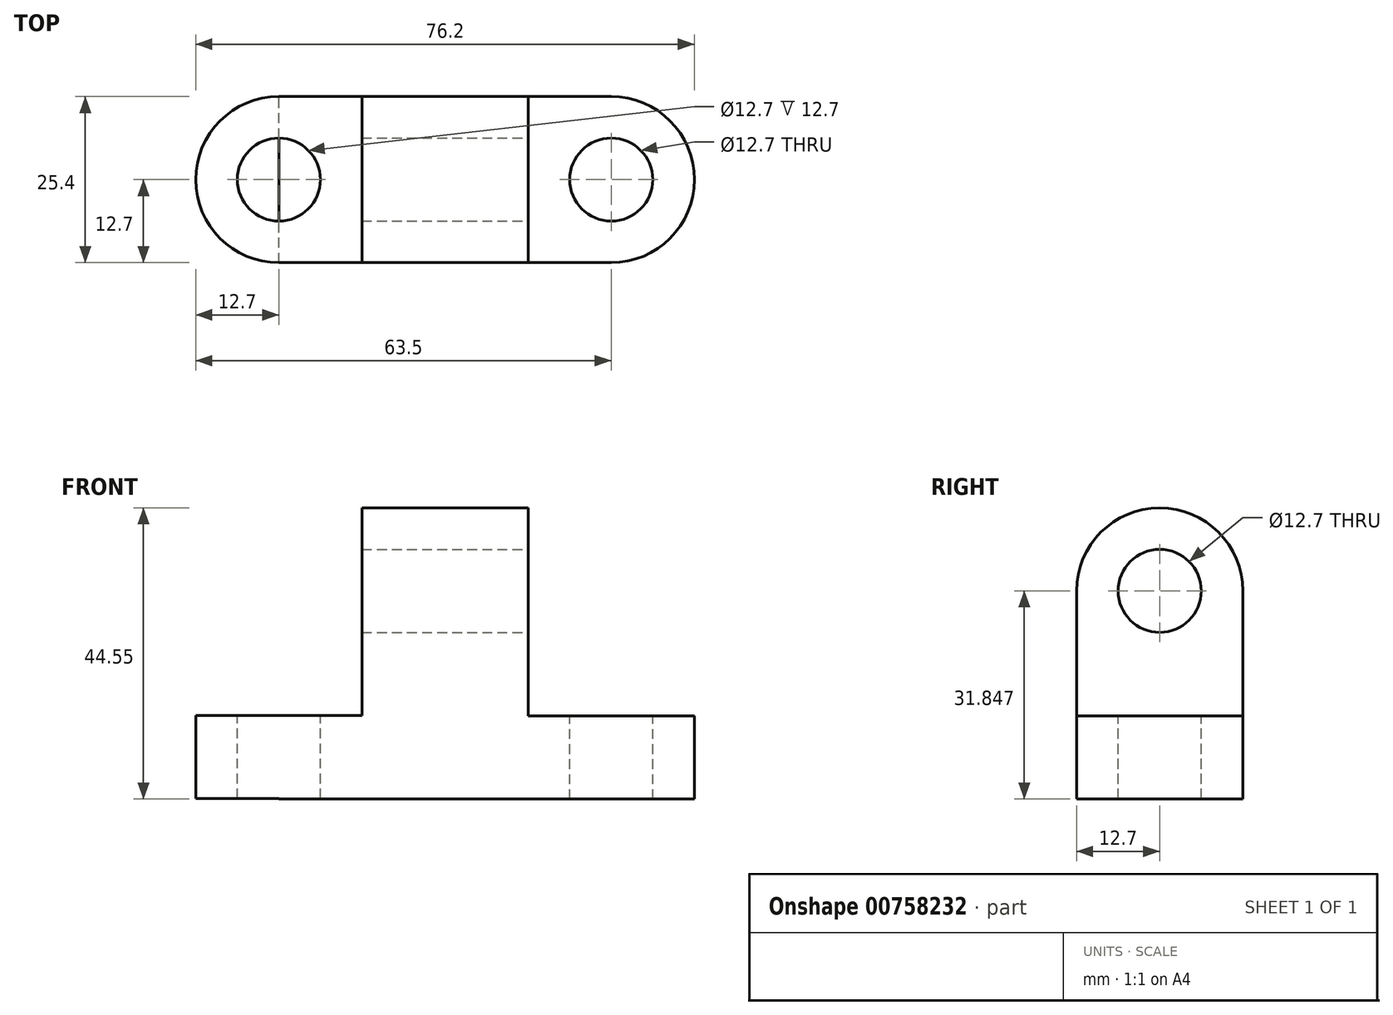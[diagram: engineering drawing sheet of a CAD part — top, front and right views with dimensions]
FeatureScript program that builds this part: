
annotation { "Feature Type Name" : "Feature", "Feature Type Description" : "" }
export const myFeature = defineFeature(function(context is Context, id is Id, definition is map)
    precondition{}
    {
        {
            var Q0;
            Q0=qCreatedBy(makeId("Front.planeOp"),FACE);
            var sketch = newSketch(context, id + "F0", { "sketchPlane" : qUnion([Q0])});
            skLineSegment(sketch, "E0", {"start": v(0, 0) * mm, "end": v(50.8, 0) * mm});
            skLineSegment(sketch, "E1", {"start": v(50.8, 0) * mm, "end": v(50.8, 12.7) * mm});
            skLineSegment(sketch, "E2", {"start": v(50.8, 12.7) * mm, "end": v(38.1, 12.7) * mm});
            skLineSegment(sketch, "E3", {"start": v(38.1, 12.7) * mm, "end": v(38.1, 31.85) * mm});
            skLineSegment(sketch, "E4", {"start": v(38.1, 31.85) * mm, "end": v(12.7, 31.85) * mm});
            skLineSegment(sketch, "E5", {"start": v(12.7, 31.85) * mm, "end": v(12.7, 12.8) * mm});
            skLineSegment(sketch, "E6", {"start": v(12.7, 12.8) * mm, "end": v(0, 12.8) * mm});
            skLineSegment(sketch, "E7", {"start": v(0, 12.8) * mm, "end": v(0, 0) * mm});
            skSolve(sketch);
        }
        {
            var Q0;
            Q0=makeQuery(id+"F0.imprint","IMPRINT",FACE,{"disambiguationData":[TD([[makeQuery(id+"F0.imprint","IMPRINT",EDGE,{"derivedFrom":sQuery(id+"F0.wireOp",EDGE,"E0")}),1.0]])]});
            extrude(context, id + "F1", {"entities" : qUnion([Q0]), "depth" : 25.4 * mm, "offsetDistance" : 25.4 * mm});
        }
        {
            var Q0;
            Q0=makeQuery(id+"F1.opExtrude","SWEPT_FACE",FACE,{"disambiguationData":[OSD([sQuery(id+"F0.wireOp",EDGE,"E3")])]});
            var sketch = newSketch(context, id + "F2", { "sketchPlane" : qUnion([Q0])});
            skArc(sketch, "E8", {"start": v(0, 31.85) * mm, "mid": v(-12.7, 44.55) * mm, "end": v(-25.4, 31.85) * mm});
            skSolve(sketch);
        }
        {
            var Q0;
            Q0=makeQuery(id+"F1.opExtrude","SWEPT_FACE",FACE,{"disambiguationData":[OSD([sQuery(id+"F0.wireOp",EDGE,"E6")])]});
            var sketch = newSketch(context, id + "F3", { "sketchPlane" : qUnion([Q0])});
            skArc(sketch, "E9", {"start": v(50.8, -25.4) * mm, "mid": v(63.5, -12.7) * mm, "end": v(50.8, 0) * mm});
            skArc(sketch, "E10", {"start": v(0, 0) * mm, "mid": v(-12.7, -12.7) * mm, "end": v(0, -25.4) * mm});
            skSolve(sketch);
        }
        {
            var Q0;
            Q0=makeQuery(id+"F2.imprint","IMPRINT",FACE,{"disambiguationData":[TD([[makeQuery(id+"F2.imprint","IMPRINT",EDGE,{"derivedFrom":sQuery(id+"F2.wireOp",EDGE,"E8")}),1.0]])]});
            extrude(context, id + "F4", {"entities" : qUnion([Q0]), "operationType" : NewBodyOperationType.ADD, "depth" : 0 * mm, "offsetDistance" : 25.4 * mm, "hasSecondDirection" : true, "secondDirectionOppositeDirection" : true, "secondDirectionDepth" : 25.4 * mm});
        }
        {
            var Q0;
            Q0=makeQuery(id+"F3.imprint","IMPRINT",FACE,{"disambiguationData":[TD([[makeQuery(id+"F3.imprint","IMPRINT",EDGE,{"derivedFrom":sQuery(id+"F3.wireOp",EDGE,"E10")}),1.0]])]});
            extrude(context, id + "F5", {"entities" : qUnion([Q0]), "operationType" : NewBodyOperationType.ADD, "depth" : 0 * mm, "offsetDistance" : 25.4 * mm, "hasSecondDirection" : true, "secondDirectionOppositeDirection" : true, "secondDirectionDepth" : 12.7 * mm});
        }
        {
            var Q0;
            Q0=makeQuery(id+"F1.opExtrude","SWEPT_FACE",FACE,{"disambiguationData":[OSD([sQuery(id+"F0.wireOp",EDGE,"E2")])]});
            var sketch = newSketch(context, id + "F6", { "sketchPlane" : qUnion([Q0])});
            skArc(sketch, "E11", {"start": v(50.8, -25.4) * mm, "mid": v(63.5, -12.7) * mm, "end": v(50.8, 0) * mm});
            skSolve(sketch);
        }
        {
            var Q0;
            Q0=makeQuery(id+"F6.imprint","IMPRINT",FACE,{"disambiguationData":[TD([[makeQuery(id+"F6.imprint","IMPRINT",EDGE,{"derivedFrom":sQuery(id+"F6.wireOp",EDGE,"E11")}),1.0]])]});
            extrude(context, id + "F7", {"entities" : qUnion([Q0]), "operationType" : NewBodyOperationType.ADD, "depth" : 0 * mm, "offsetDistance" : 25.4 * mm, "hasSecondDirection" : true, "secondDirectionOppositeDirection" : true, "secondDirectionDepth" : 12.7 * mm});
        }
        {
            var Q0;
            {var subQ0=sQuery(id+"F0.wireOp",EDGE,"E6");Q0=makeQuery(id+"F5.boolean.opBoolean","MERGE",FACE,{"derivedFrom":[makeQuery(id+"F1.opExtrude","SWEPT_FACE",FACE,{"disambiguationData":[OSD([subQ0])]}),makeQuery(id+"F5.opExtrude","CAP_FACE",FACE,{"disambiguationData":[OSD([subQ0,sQuery(id+"F0.wireOp",EDGE,"E7"),sQuery(id+"F3.wireOp",EDGE,"E10")])],"isStart":false})]});}
            var sketch = newSketch(context, id + "F8", { "sketchPlane" : qUnion([Q0])});
            skCircle(sketch, "E12", {"center": v(0, -12.7) * mm, "radius": 6.35 * mm});
            skSolve(sketch);
        }
        {
            var Q0;
            {var subQ0=sQuery(id+"F0.wireOp",EDGE,"E2");Q0=makeQuery(id+"F7.boolean.opBoolean","MERGE",FACE,{"derivedFrom":[makeQuery(id+"F1.opExtrude","SWEPT_FACE",FACE,{"disambiguationData":[OSD([subQ0])]}),makeQuery(id+"F7.opExtrude","CAP_FACE",FACE,{"disambiguationData":[OSD([sQuery(id+"F0.wireOp",EDGE,"E1"),subQ0,sQuery(id+"F6.wireOp",EDGE,"E11")])],"isStart":false})]});}
            var sketch = newSketch(context, id + "F9", { "sketchPlane" : qUnion([Q0])});
            skCircle(sketch, "E13", {"center": v(50.8, -12.7) * mm, "radius": 6.35 * mm});
            skSolve(sketch);
        }
        {
            var Q0;
            {var subQ0=sQuery(id+"F0.wireOp",EDGE,"E3");Q0=makeQuery(id+"F4.boolean.opBoolean","MERGE",FACE,{"derivedFrom":[makeQuery(id+"F1.opExtrude","SWEPT_FACE",FACE,{"disambiguationData":[OSD([subQ0])]}),makeQuery(id+"F4.opExtrude","CAP_FACE",FACE,{"disambiguationData":[OSD([subQ0,sQuery(id+"F0.wireOp",EDGE,"E4"),sQuery(id+"F2.wireOp",EDGE,"E8")])],"isStart":false})]});}
            var sketch = newSketch(context, id + "F10", { "sketchPlane" : qUnion([Q0])});
            skCircle(sketch, "E14", {"center": v(-12.7, 31.85) * mm, "radius": 6.35 * mm});
            skSolve(sketch);
        }
        {
            var Q0;
            Q0=makeQuery(id+"F10.imprint","IMPRINT",FACE,{"disambiguationData":[TD([[makeQuery(id+"F10.imprint","IMPRINT",EDGE,{"derivedFrom":sQuery(id+"F10.wireOp",EDGE,"E14")}),1.0]])]});
            extrude(context, id + "F11", {"entities" : qUnion([Q0]), "operationType" : NewBodyOperationType.REMOVE, "oppositeDirection" : true, "depth" : 25.4 * mm, "offsetDistance" : 25.4 * mm});
        }
        {
            var Q0;
            Q0=makeQuery(id+"F8.imprint","IMPRINT",FACE,{"disambiguationData":[TD([[makeQuery(id+"F8.imprint","IMPRINT",EDGE,{"derivedFrom":sQuery(id+"F8.wireOp",EDGE,"E12")}),1.0]])]});
            var Q1;
            Q1=makeQuery(id+"F9.imprint","IMPRINT",FACE,{"disambiguationData":[TD([[makeQuery(id+"F9.imprint","IMPRINT",EDGE,{"derivedFrom":sQuery(id+"F9.wireOp",EDGE,"E13")}),1.0]])]});
            extrude(context, id + "F12", {"entities" : qUnion([Q0, Q1]), "operationType" : NewBodyOperationType.REMOVE, "oppositeDirection" : true, "depth" : 12.7 * mm, "offsetDistance" : 25.4 * mm});
        }
    });
